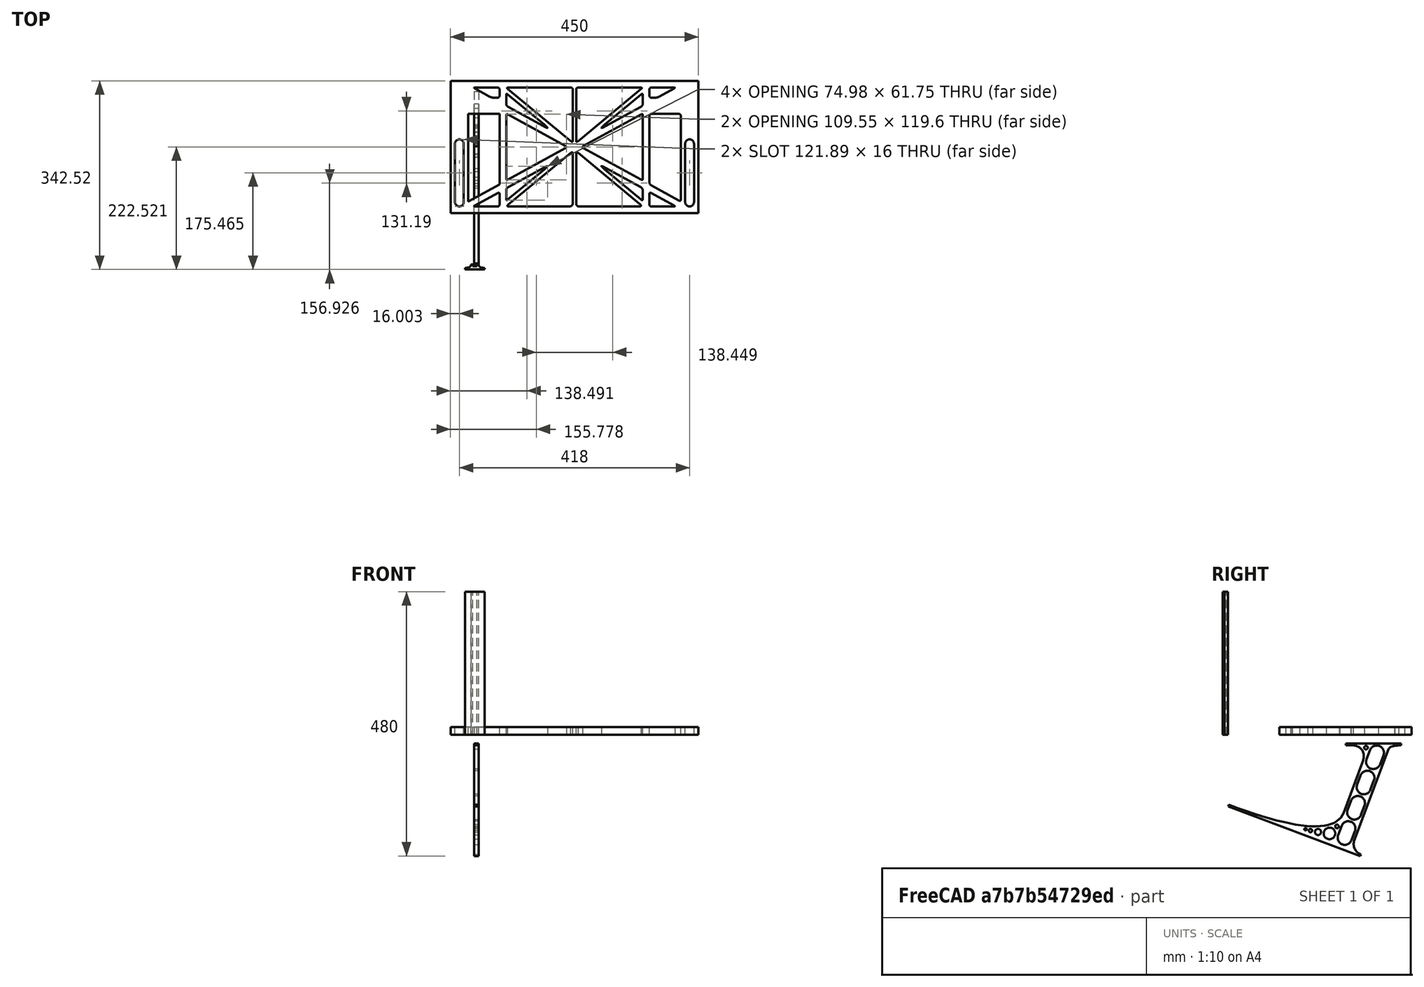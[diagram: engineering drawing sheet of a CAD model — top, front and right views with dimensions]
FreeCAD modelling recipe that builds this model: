
FCSTD DOCUMENT  (FreeCAD 0.19R0.19.2)
Label: laptopStand137FCStd
License: All rights reserved
LicenseURL: http://en.wikipedia.org/wiki/All_rights_reserved
objects: Sketcher::SketchObject×3, Part::Extrusion×3
note: 6 computed .brp shape members not serialized (recipe doc carries the construction recipe); baked Part::Feature solids carry a one-line shape summary decoded from their .brp

FEATURE [Sketcher::SketchObject] Sketch
  FullyConstrained = false
  sketch-geometry (349):
    g0: LineSegment StartX=-10.9272 StartY=-82.7794 StartZ=0 EndX=46.0728 EndY=-51.4823 EndZ=0
    g1: LineSegment StartX=-10.9272 StartY=76.4095 StartZ=0 EndX=-10.9272 EndY=-82.7794 EndZ=0
    g2: LineSegment StartX=46.0728 StartY=76.4095 StartZ=0 EndX=46.0728 EndY=-51.4823 EndZ=0
    g3: LineSegment StartX=-42.9272 StartY=136.221 StartZ=0 EndX=-42.9272 EndY=-103.779 EndZ=0
    g4: LineSegment StartX=407.073 StartY=136.221 StartZ=0 EndX=407.073 EndY=-103.779 EndZ=0
    g5: ArcOfCircle CenterX=-26.9272 CenterY=-83.7794 CenterZ=0 NormalX=0 NormalY=0 NormalZ=1 AngleXU=0 Radius=8 StartAngle=3.14159 EndAngle=6.28319
    g6: ArcOfCircle CenterX=391.073 CenterY=22.1087 CenterZ=0 NormalX=0 NormalY=0 NormalZ=1 AngleXU=0 Radius=8 StartAngle=-4.4e-15 EndAngle=3.14159
    g7: LineSegment StartX=399.073 StartY=22.1087 StartZ=0 EndX=399.073 EndY=-83.7794 EndZ=0
    g8: LineSegment StartX=383.073 StartY=22.1087 StartZ=0 EndX=383.073 EndY=-83.7794 EndZ=0
    g9: ArcOfCircle CenterX=391.073 CenterY=-83.7794 CenterZ=0 NormalX=0 NormalY=0 NormalZ=1 AngleXU=0 Radius=8 StartAngle=3.14159 EndAngle=6.28319
    g10: Circle CenterX=175.022 CenterY=27.0628 CenterZ=0 NormalX=0 NormalY=0 NormalZ=1 AngleXU=0 Radius=1
    g11: Circle CenterX=179.022 CenterY=24.8665 CenterZ=0 NormalX=0 NormalY=0 NormalZ=1 AngleXU=0 Radius=1
    g12: Circle CenterX=179.022 CenterY=27.0628 CenterZ=0 NormalX=0 NormalY=0 NormalZ=1 AngleXU=0 Radius=1
    g13: BSplineCurve PolesCount=3 KnotsCount=2 Degree=2 IsPeriodic=0
    g14: GeomPoint X=175.022 Y=27.0628 Z=0
    g15: GeomPoint X=179.022 Y=27.0628 Z=0
    g16: Circle CenterX=189.124 CenterY=27.0628 CenterZ=0 NormalX=0 NormalY=0 NormalZ=1 AngleXU=0 Radius=1
    g17: Circle CenterX=185.124 CenterY=24.8665 CenterZ=0 NormalX=0 NormalY=0 NormalZ=1 AngleXU=0 Radius=1
    g18: Circle CenterX=185.124 CenterY=27.0628 CenterZ=0 NormalX=0 NormalY=0 NormalZ=1 AngleXU=0 Radius=1
    g19: BSplineCurve PolesCount=3 KnotsCount=2 Degree=2 IsPeriodic=0
    g20: GeomPoint X=189.124 Y=27.0628 Z=0
    g21: GeomPoint X=185.124 Y=27.0628 Z=0
    g22: Circle CenterX=175.022 CenterY=5.37834 CenterZ=0 NormalX=0 NormalY=0 NormalZ=1 AngleXU=0 Radius=1
    g23: Circle CenterX=179.022 CenterY=7.57463 CenterZ=0 NormalX=0 NormalY=0 NormalZ=1 AngleXU=0 Radius=1
    g24: Circle CenterX=179.022 CenterY=5.34704 CenterZ=0 NormalX=0 NormalY=0 NormalZ=1 AngleXU=0 Radius=1
    g25: BSplineCurve PolesCount=3 KnotsCount=2 Degree=2 IsPeriodic=0
    g26: GeomPoint X=175.022 Y=5.37834 Z=0
    g27: GeomPoint X=179.022 Y=5.34704 Z=0
    g28: Circle CenterX=189.124 CenterY=5.37834 CenterZ=0 NormalX=0 NormalY=0 NormalZ=1 AngleXU=0 Radius=1
    g29: Circle CenterX=185.124 CenterY=7.57463 CenterZ=0 NormalX=0 NormalY=0 NormalZ=1 AngleXU=0 Radius=1
    g30: Circle CenterX=185.124 CenterY=5.34704 CenterZ=0 NormalX=0 NormalY=0 NormalZ=1 AngleXU=0 Radius=1
    g31: BSplineCurve PolesCount=3 KnotsCount=2 Degree=2 IsPeriodic=0
    g32: GeomPoint X=189.124 Y=5.37834 Z=0
    g33: GeomPoint X=185.124 Y=5.34704 Z=0
    g34: Circle CenterX=165.871 CenterY=18.1458 CenterZ=0 NormalX=0 NormalY=0 NormalZ=1 AngleXU=0 Radius=1
    g35: Circle CenterX=169.377 CenterY=16.2206 CenterZ=0 NormalX=0 NormalY=0 NormalZ=1 AngleXU=0 Radius=1
    g36: Circle CenterX=165.871 CenterY=14.2954 CenterZ=0 NormalX=0 NormalY=0 NormalZ=1 AngleXU=0 Radius=1
    g37: BSplineCurve PolesCount=3 KnotsCount=2 Degree=2 IsPeriodic=0
    g38: GeomPoint X=165.871 Y=18.1458 Z=0
    g39: GeomPoint X=165.871 Y=14.2954 Z=0
    g40: Circle CenterX=198.275 CenterY=18.1458 CenterZ=0 NormalX=0 NormalY=0 NormalZ=1 AngleXU=0 Radius=1
    g41: Circle CenterX=194.768 CenterY=16.2206 CenterZ=0 NormalX=0 NormalY=0 NormalZ=1 AngleXU=0 Radius=1
    g42: Circle CenterX=198.275 CenterY=14.2954 CenterZ=0 NormalX=0 NormalY=0 NormalZ=1 AngleXU=0 Radius=1
    g43: BSplineCurve PolesCount=3 KnotsCount=2 Degree=2 IsPeriodic=0
    g44: GeomPoint X=198.275 Y=18.1458 Z=0
    g45: GeomPoint X=198.275 Y=14.2954 Z=0
    g46: LineSegment StartX=407.073 StartY=-103.779 StartZ=0 EndX=-42.9272 EndY=-103.779 EndZ=0
    g47: LineSegment StartX=407.073 StartY=136.221 StartZ=0 EndX=-42.9272 EndY=136.221 EndZ=0
    g48: LineSegment StartX=46.0728 StartY=76.4095 StartZ=0 EndX=-10.9272 EndY=76.4095 EndZ=0
    g49: Circle CenterX=125.607 CenterY=54.1951 CenterZ=0 NormalX=0 NormalY=0 NormalZ=1 AngleXU=0 Radius=1
    g50: Circle CenterX=139.632 CenterY=46.4944 CenterZ=0 NormalX=0 NormalY=0 NormalZ=1 AngleXU=0 Radius=1
    g51: Circle CenterX=127.326 CenterY=56.7187 CenterZ=0 NormalX=0 NormalY=0 NormalZ=1 AngleXU=0 Radius=1
    g52: BSplineCurve PolesCount=3 KnotsCount=2 Degree=2 IsPeriodic=0
    g53: GeomPoint X=125.607 Y=54.1951 Z=0
    g54: GeomPoint X=127.326 Y=56.7187 Z=0
    g55: Circle CenterX=236.821 CenterY=56.7187 CenterZ=0 NormalX=0 NormalY=0 NormalZ=1 AngleXU=0 Radius=1
    g56: Circle CenterX=224.513 CenterY=46.4944 CenterZ=0 NormalX=0 NormalY=0 NormalZ=1 AngleXU=0 Radius=1
    g57: Circle CenterX=238.538 CenterY=54.1951 CenterZ=0 NormalX=0 NormalY=0 NormalZ=1 AngleXU=0 Radius=1
    g58: BSplineCurve PolesCount=3 KnotsCount=2 Degree=2 IsPeriodic=0
    g59: GeomPoint X=236.821 Y=56.7187 Z=0
    g60: GeomPoint X=238.538 Y=54.1951 Z=0
    g61: Circle CenterX=238.538 CenterY=-21.7539 CenterZ=0 NormalX=0 NormalY=0 NormalZ=1 AngleXU=0 Radius=1
    g62: Circle CenterX=224.513 CenterY=-14.0532 CenterZ=0 NormalX=0 NormalY=0 NormalZ=1 AngleXU=0 Radius=1
    g63: Circle CenterX=236.821 CenterY=-24.2775 CenterZ=0 NormalX=0 NormalY=0 NormalZ=1 AngleXU=0 Radius=1
    g64: BSplineCurve PolesCount=3 KnotsCount=2 Degree=2 IsPeriodic=0
    g65: GeomPoint X=238.538 Y=-21.7539 Z=0
    g66: GeomPoint X=236.821 Y=-24.2775 Z=0
    g67: Circle CenterX=125.607 CenterY=-21.7539 CenterZ=0 NormalX=0 NormalY=0 NormalZ=1 AngleXU=0 Radius=1
    g68: Circle CenterX=139.632 CenterY=-14.0532 CenterZ=0 NormalX=0 NormalY=0 NormalZ=1 AngleXU=0 Radius=1
    g69: Circle CenterX=127.325 CenterY=-24.2775 CenterZ=0 NormalX=0 NormalY=0 NormalZ=1 AngleXU=0 Radius=1
    g70: BSplineCurve PolesCount=3 KnotsCount=2 Degree=2 IsPeriodic=0
    g71: GeomPoint X=125.607 Y=-21.7539 Z=0
    g72: GeomPoint X=127.325 Y=-24.2775 Z=0
    g73: Circle CenterX=302.996 CenterY=111.695 CenterZ=0 NormalX=0 NormalY=0 NormalZ=1 AngleXU=0 Radius=1
    g74: Circle CenterX=306.073 CenterY=114.251 CenterZ=0 NormalX=0 NormalY=0 NormalZ=1 AngleXU=0 Radius=1
    g75: Circle CenterX=306.073 CenterY=110.251 CenterZ=0 NormalX=0 NormalY=0 NormalZ=1 AngleXU=0 Radius=1
    g76: BSplineCurve PolesCount=3 KnotsCount=2 Degree=2 IsPeriodic=0
    g77: GeomPoint X=302.996 Y=111.695 Z=0
    g78: GeomPoint X=306.073 Y=110.251 Z=0
    g79: Circle CenterX=306.073 CenterY=95.2763 CenterZ=0 NormalX=0 NormalY=0 NormalZ=1 AngleXU=0 Radius=1
    g80: Circle CenterX=306.073 CenterY=91.2763 CenterZ=0 NormalX=0 NormalY=0 NormalZ=1 AngleXU=0 Radius=1
    g81: Circle CenterX=302.567 CenterY=89.3511 CenterZ=0 NormalX=0 NormalY=0 NormalZ=1 AngleXU=0 Radius=1
    g82: BSplineCurve PolesCount=3 KnotsCount=2 Degree=2 IsPeriodic=0
    g83: GeomPoint X=306.073 Y=95.2763 Z=0
    g84: GeomPoint X=302.567 Y=89.3511 Z=0
    g85: LineSegment StartX=306.073 StartY=110.251 StartZ=0 EndX=306.073 EndY=95.2763 EndZ=0
    g86: LineSegment StartX=302.996 StartY=111.695 StartZ=0 EndX=236.821 EndY=56.7187 EndZ=0
    g87: LineSegment StartX=238.538 StartY=54.1951 StartZ=0 EndX=302.567 EndY=89.3511 EndZ=0
    g88: Circle CenterX=61.1496 CenterY=111.695 CenterZ=0 NormalX=0 NormalY=0 NormalZ=1 AngleXU=0 Radius=1
    g89: Circle CenterX=58.0728 CenterY=114.251 CenterZ=0 NormalX=0 NormalY=0 NormalZ=1 AngleXU=0 Radius=1
    g90: Circle CenterX=58.0728 CenterY=110.251 CenterZ=0 NormalX=0 NormalY=0 NormalZ=1 AngleXU=0 Radius=1
    g91: BSplineCurve PolesCount=3 KnotsCount=2 Degree=2 IsPeriodic=0
    g92: GeomPoint X=61.1496 Y=111.695 Z=0
    g93: GeomPoint X=58.0728 Y=110.251 Z=0
    g94: Circle CenterX=61.5791 CenterY=89.3511 CenterZ=0 NormalX=0 NormalY=0 NormalZ=1 AngleXU=0 Radius=1
    g95: Circle CenterX=58.0728 CenterY=91.2763 CenterZ=0 NormalX=0 NormalY=0 NormalZ=1 AngleXU=0 Radius=1
    g96: Circle CenterX=58.0728 CenterY=95.2763 CenterZ=0 NormalX=0 NormalY=0 NormalZ=1 AngleXU=0 Radius=1
    g97: BSplineCurve PolesCount=3 KnotsCount=2 Degree=2 IsPeriodic=0
    g98: GeomPoint X=61.5791 Y=89.3511 Z=0
    g99: GeomPoint X=58.0728 Y=95.2763 Z=0
    g100: LineSegment StartX=58.0728 StartY=110.251 StartZ=0 EndX=58.0728 EndY=95.2763 EndZ=0
    g101: LineSegment StartX=61.1496 StartY=111.695 StartZ=0 EndX=127.326 EndY=56.7187 EndZ=0
    g102: LineSegment StartX=125.607 StartY=54.1951 StartZ=0 EndX=61.5791 EndY=89.3511 EndZ=0
    g103: Circle CenterX=61.5791 CenterY=-56.9099 CenterZ=0 NormalX=0 NormalY=0 NormalZ=1 AngleXU=0 Radius=1
    g104: Circle CenterX=58.0728 CenterY=-58.8351 CenterZ=0 NormalX=0 NormalY=0 NormalZ=1 AngleXU=0 Radius=1
    g105: Circle CenterX=58.0728 CenterY=-62.8351 CenterZ=0 NormalX=0 NormalY=0 NormalZ=1 AngleXU=0 Radius=1
    g106: BSplineCurve PolesCount=3 KnotsCount=2 Degree=2 IsPeriodic=0
    g107: GeomPoint X=61.5791 Y=-56.9099 Z=0
    g108: GeomPoint X=58.0728 Y=-62.8351 Z=0
    g109: Circle CenterX=58.0728 CenterY=-77.8102 CenterZ=0 NormalX=0 NormalY=0 NormalZ=1 AngleXU=0 Radius=1
    g110: Circle CenterX=58.0728 CenterY=-81.8102 CenterZ=0 NormalX=0 NormalY=0 NormalZ=1 AngleXU=0 Radius=1
    g111: Circle CenterX=61.1496 CenterY=-79.2541 CenterZ=0 NormalX=0 NormalY=0 NormalZ=1 AngleXU=0 Radius=1
    g112: BSplineCurve PolesCount=3 KnotsCount=2 Degree=2 IsPeriodic=0
    g113: GeomPoint X=58.0728 Y=-77.8102 Z=0
    g114: GeomPoint X=61.1496 Y=-79.2541 Z=0
    g115: LineSegment StartX=58.0728 StartY=-62.8351 StartZ=0 EndX=58.0728 EndY=-77.8102 EndZ=0
    g116: LineSegment StartX=61.1496 StartY=-79.2541 StartZ=0 EndX=127.325 EndY=-24.2775 EndZ=0
    g117: LineSegment StartX=125.607 StartY=-21.7539 StartZ=0 EndX=61.5791 EndY=-56.9099 EndZ=0
    g118: Circle CenterX=302.567 CenterY=-56.9099 CenterZ=0 NormalX=0 NormalY=0 NormalZ=1 AngleXU=0 Radius=1
    g119: Circle CenterX=306.073 CenterY=-58.8351 CenterZ=0 NormalX=0 NormalY=0 NormalZ=1 AngleXU=0 Radius=1
    g120: Circle CenterX=306.073 CenterY=-62.8351 CenterZ=0 NormalX=0 NormalY=0 NormalZ=1 AngleXU=0 Radius=1
    g121: BSplineCurve PolesCount=3 KnotsCount=2 Degree=2 IsPeriodic=0
    g122: GeomPoint X=302.567 Y=-56.9099 Z=0
    g123: GeomPoint X=306.073 Y=-62.8351 Z=0
    g124: Circle CenterX=302.996 CenterY=-79.2541 CenterZ=0 NormalX=0 NormalY=0 NormalZ=1 AngleXU=0 Radius=1
    g125: Circle CenterX=306.073 CenterY=-81.8102 CenterZ=0 NormalX=0 NormalY=0 NormalZ=1 AngleXU=0 Radius=1
    g126: Circle CenterX=306.073 CenterY=-77.8102 CenterZ=0 NormalX=0 NormalY=0 NormalZ=1 AngleXU=0 Radius=1
    g127: BSplineCurve PolesCount=3 KnotsCount=2 Degree=2 IsPeriodic=0
    g128: GeomPoint X=302.996 Y=-79.2541 Z=0
    g129: GeomPoint X=306.073 Y=-77.8102 Z=0
    g130: LineSegment StartX=306.073 StartY=-62.8351 StartZ=0 EndX=306.073 EndY=-77.8102 EndZ=0
    g131: LineSegment StartX=302.996 StartY=-79.2541 StartZ=0 EndX=236.821 EndY=-24.2775 EndZ=0
    g132: LineSegment StartX=238.538 StartY=-21.7539 StartZ=0 EndX=302.567 EndY=-56.9099 EndZ=0
    g133: Circle CenterX=61.6457 CenterY=-88.8112 CenterZ=0 NormalX=0 NormalY=0 NormalZ=1 AngleXU=0 Radius=1
    g134: Circle CenterX=58.0728 CenterY=-91.7794 CenterZ=0 NormalX=0 NormalY=0 NormalZ=1 AngleXU=0 Radius=1
    g135: Circle CenterX=63.9135 CenterY=-91.7794 CenterZ=0 NormalX=0 NormalY=0 NormalZ=1 AngleXU=0 Radius=1
    g136: BSplineCurve PolesCount=3 KnotsCount=2 Degree=2 IsPeriodic=0
    g137: GeomPoint X=61.6457 Y=-88.8112 Z=0
    g138: GeomPoint X=63.9135 Y=-91.7794 Z=0
    g139: Circle CenterX=179.022 CenterY=-85.8163 CenterZ=0 NormalX=0 NormalY=0 NormalZ=1 AngleXU=0 Radius=1
    g140: Circle CenterX=179.022 CenterY=-91.7794 CenterZ=0 NormalX=0 NormalY=0 NormalZ=1 AngleXU=0 Radius=1
    g141: Circle CenterX=171.895 CenterY=-91.7794 CenterZ=0 NormalX=0 NormalY=0 NormalZ=1 AngleXU=0 Radius=1
    g142: BSplineCurve PolesCount=3 KnotsCount=2 Degree=2 IsPeriodic=0
    g143: GeomPoint X=179.022 Y=-85.8163 Z=0
    g144: GeomPoint X=171.895 Y=-91.7794 Z=0
    g145: Circle CenterX=185.124 CenterY=-86.2028 CenterZ=0 NormalX=0 NormalY=0 NormalZ=1 AngleXU=0 Radius=1
    g146: Circle CenterX=185.124 CenterY=-91.7794 CenterZ=0 NormalX=0 NormalY=0 NormalZ=1 AngleXU=0 Radius=1
    g147: Circle CenterX=191.747 CenterY=-91.7794 CenterZ=0 NormalX=0 NormalY=0 NormalZ=1 AngleXU=0 Radius=1
    g148: BSplineCurve PolesCount=3 KnotsCount=2 Degree=2 IsPeriodic=0
    g149: GeomPoint X=185.124 Y=-86.2028 Z=0
    g150: GeomPoint X=191.747 Y=-91.7794 Z=0
    g151: Circle CenterX=299.888 CenterY=-86.6413 CenterZ=0 NormalX=0 NormalY=0 NormalZ=1 AngleXU=0 Radius=1
    g152: Circle CenterX=306.073 CenterY=-91.7794 CenterZ=0 NormalX=0 NormalY=0 NormalZ=1 AngleXU=0 Radius=1
    g153: Circle CenterX=298.776 CenterY=-91.7794 CenterZ=0 NormalX=0 NormalY=0 NormalZ=1 AngleXU=0 Radius=1
    g154: BSplineCurve PolesCount=3 KnotsCount=2 Degree=2 IsPeriodic=0
    g155: GeomPoint X=299.888 Y=-86.6413 Z=0
    g156: GeomPoint X=298.776 Y=-91.7794 Z=0
    g157: LineSegment StartX=189.124 StartY=5.37834 StartZ=0 EndX=299.888 EndY=-86.6413 EndZ=0
    g158: LineSegment StartX=298.776 StartY=-91.7794 StartZ=0 EndX=191.747 EndY=-91.7794 EndZ=0
    g159: LineSegment StartX=185.124 StartY=-86.2028 StartZ=0 EndX=185.124 EndY=5.34704 EndZ=0
    g160: LineSegment StartX=179.022 StartY=5.34704 StartZ=0 EndX=179.022 EndY=-85.8163 EndZ=0
    g161: LineSegment StartX=171.895 StartY=-91.7794 StartZ=0 EndX=63.9135 EndY=-91.7794 EndZ=0
    g162: LineSegment StartX=61.6457 StartY=-88.8112 StartZ=0 EndX=175.022 EndY=5.37834 EndZ=0
    g163: Circle CenterX=302.073 CenterY=124.221 CenterZ=0 NormalX=0 NormalY=0 NormalZ=1 AngleXU=0 Radius=1
    g164: Circle CenterX=306.073 CenterY=124.221 CenterZ=0 NormalX=0 NormalY=0 NormalZ=1 AngleXU=0 Radius=1
    g165: Circle CenterX=302.996 CenterY=121.665 CenterZ=0 NormalX=0 NormalY=0 NormalZ=1 AngleXU=0 Radius=1
    g166: BSplineCurve PolesCount=3 KnotsCount=2 Degree=2 IsPeriodic=0
    g167: GeomPoint X=302.073 Y=124.221 Z=0
    g168: GeomPoint X=302.996 Y=121.665 Z=0
    g169: Circle CenterX=189.124 CenterY=124.221 CenterZ=0 NormalX=0 NormalY=0 NormalZ=1 AngleXU=0 Radius=1
    g170: Circle CenterX=185.124 CenterY=124.221 CenterZ=0 NormalX=0 NormalY=0 NormalZ=1 AngleXU=0 Radius=1
    g171: Circle CenterX=185.124 CenterY=120.221 CenterZ=0 NormalX=0 NormalY=0 NormalZ=1 AngleXU=0 Radius=1
    g172: BSplineCurve PolesCount=3 KnotsCount=2 Degree=2 IsPeriodic=0
    g173: GeomPoint X=189.124 Y=124.221 Z=0
    g174: GeomPoint X=185.124 Y=120.221 Z=0
    g175: Circle CenterX=175.022 CenterY=124.221 CenterZ=0 NormalX=0 NormalY=0 NormalZ=1 AngleXU=0 Radius=1
    g176: Circle CenterX=179.022 CenterY=124.221 CenterZ=0 NormalX=0 NormalY=0 NormalZ=1 AngleXU=0 Radius=1
    g177: Circle CenterX=179.022 CenterY=120.221 CenterZ=0 NormalX=0 NormalY=0 NormalZ=1 AngleXU=0 Radius=1
    g178: BSplineCurve PolesCount=3 KnotsCount=2 Degree=2 IsPeriodic=0
    g179: GeomPoint X=175.022 Y=124.221 Z=0
    g180: GeomPoint X=179.022 Y=120.221 Z=0
    g181: Circle CenterX=62.0728 CenterY=124.221 CenterZ=0 NormalX=0 NormalY=0 NormalZ=1 AngleXU=0 Radius=1
    g182: Circle CenterX=58.0728 CenterY=124.221 CenterZ=0 NormalX=0 NormalY=0 NormalZ=1 AngleXU=0 Radius=1
    g183: Circle CenterX=61.1496 CenterY=121.665 CenterZ=0 NormalX=0 NormalY=0 NormalZ=1 AngleXU=0 Radius=1
    g184: BSplineCurve PolesCount=3 KnotsCount=2 Degree=2 IsPeriodic=0
    g185: GeomPoint X=62.0728 Y=124.221 Z=0
    g186: GeomPoint X=61.1496 Y=121.665 Z=0
    g187: LineSegment StartX=62.0728 StartY=124.221 StartZ=0 EndX=175.022 EndY=124.221 EndZ=0
    g188: LineSegment StartX=179.022 StartY=120.221 StartZ=0 EndX=179.022 EndY=27.0628 EndZ=0
    g189: LineSegment StartX=185.124 StartY=27.0628 StartZ=0 EndX=185.124 EndY=120.221 EndZ=0
    g190: LineSegment StartX=189.124 StartY=124.221 StartZ=0 EndX=302.073 EndY=124.221 EndZ=0
    g191: LineSegment StartX=302.996 StartY=121.665 StartZ=0 EndX=189.124 EndY=27.0628 EndZ=0
    g192: LineSegment StartX=175.022 StartY=27.0628 StartZ=0 EndX=61.1496 EndY=121.665 EndZ=0
    g193: Circle CenterX=61.5791 CenterY=75.4095 CenterZ=0 NormalX=0 NormalY=0 NormalZ=1 AngleXU=0 Radius=1
    g194: Circle CenterX=58.0728 CenterY=77.3346 CenterZ=0 NormalX=0 NormalY=0 NormalZ=1 AngleXU=0 Radius=1
    g195: Circle CenterX=58.0728 CenterY=73.3346 CenterZ=0 NormalX=0 NormalY=0 NormalZ=1 AngleXU=0 Radius=1
    g196: BSplineCurve PolesCount=3 KnotsCount=2 Degree=2 IsPeriodic=0
    g197: GeomPoint X=61.5791 Y=75.4095 Z=0
    g198: GeomPoint X=58.0728 Y=73.3346 Z=0
    g199: Circle CenterX=58.0728 CenterY=-40.8935 CenterZ=0 NormalX=0 NormalY=0 NormalZ=1 AngleXU=0 Radius=1
    g200: Circle CenterX=58.0728 CenterY=-44.8935 CenterZ=0 NormalX=0 NormalY=0 NormalZ=1 AngleXU=0 Radius=1
    g201: Circle CenterX=61.5791 CenterY=-42.9683 CenterZ=0 NormalX=0 NormalY=0 NormalZ=1 AngleXU=0 Radius=1
    g202: BSplineCurve PolesCount=3 KnotsCount=2 Degree=2 IsPeriodic=0
    g203: GeomPoint X=58.0728 Y=-40.8935 Z=0
    g204: GeomPoint X=61.5791 Y=-42.9683 Z=0
    g205: LineSegment StartX=61.5791 StartY=-42.9683 StartZ=0 EndX=165.871 EndY=14.2954 EndZ=0
    g206: LineSegment StartX=165.871 StartY=18.1458 StartZ=0 EndX=61.5791 EndY=75.4095 EndZ=0
    g207: LineSegment StartX=58.0728 StartY=73.3346 StartZ=0 EndX=58.0728 EndY=-40.8935 EndZ=0
    g208: Circle CenterX=302.567 CenterY=-42.9683 CenterZ=0 NormalX=0 NormalY=0 NormalZ=1 AngleXU=0 Radius=1
    g209: Circle CenterX=306.073 CenterY=-44.8935 CenterZ=0 NormalX=0 NormalY=0 NormalZ=1 AngleXU=0 Radius=1
    g210: Circle CenterX=306.073 CenterY=-40.8935 CenterZ=0 NormalX=0 NormalY=0 NormalZ=1 AngleXU=0 Radius=1
    g211: BSplineCurve PolesCount=3 KnotsCount=2 Degree=2 IsPeriodic=0
    g212: GeomPoint X=302.567 Y=-42.9683 Z=0
    g213: GeomPoint X=306.073 Y=-40.8935 Z=0
    g214: Circle CenterX=306.073 CenterY=73.3346 CenterZ=0 NormalX=0 NormalY=0 NormalZ=1 AngleXU=0 Radius=1
    g215: Circle CenterX=306.073 CenterY=77.3346 CenterZ=0 NormalX=0 NormalY=0 NormalZ=1 AngleXU=0 Radius=1
    g216: Circle CenterX=302.567 CenterY=75.4095 CenterZ=0 NormalX=0 NormalY=0 NormalZ=1 AngleXU=0 Radius=1
    g217: BSplineCurve PolesCount=3 KnotsCount=2 Degree=2 IsPeriodic=0
    g218: GeomPoint X=306.073 Y=73.3346 Z=0
    g219: GeomPoint X=302.567 Y=75.4095 Z=0
    g220: LineSegment StartX=302.567 StartY=-42.9683 StartZ=0 EndX=198.275 EndY=14.2954 EndZ=0
    g221: LineSegment StartX=198.275 StartY=18.1458 StartZ=0 EndX=302.567 EndY=75.4095 EndZ=0
    g222: LineSegment StartX=306.073 StartY=73.3346 StartZ=0 EndX=306.073 EndY=-40.8935 EndZ=0
    g223: LineSegment StartX=322.073 StartY=105.865 StartZ=0 EndX=328.643 EndY=105.865 EndZ=0
    g224: LineSegment StartX=318.073 StartY=120.221 StartZ=0 EndX=318.073 EndY=109.865 EndZ=0
    g225: LineSegment StartX=336.157 StartY=107.779 StartZ=0 EndX=362.567 EndY=122.294 EndZ=0
    g226: Circle CenterX=362.073 CenterY=124.221 CenterZ=0 NormalX=0 NormalY=0 NormalZ=1 AngleXU=0 Radius=1
    g227: Circle CenterX=366.073 CenterY=124.221 CenterZ=0 NormalX=0 NormalY=0 NormalZ=1 AngleXU=0 Radius=1
    g228: Circle CenterX=362.567 CenterY=122.294 CenterZ=0 NormalX=0 NormalY=0 NormalZ=1 AngleXU=0 Radius=1
    g229: BSplineCurve PolesCount=3 KnotsCount=2 Degree=2 IsPeriodic=0
    g230: GeomPoint X=362.073 Y=124.221 Z=0
    g231: GeomPoint X=362.567 Y=122.294 Z=0
    g232: Circle CenterX=322.073 CenterY=124.221 CenterZ=0 NormalX=0 NormalY=0 NormalZ=1 AngleXU=0 Radius=1
    g233: Circle CenterX=318.073 CenterY=124.221 CenterZ=0 NormalX=0 NormalY=0 NormalZ=1 AngleXU=0 Radius=1
    g234: Circle CenterX=318.073 CenterY=120.221 CenterZ=0 NormalX=0 NormalY=0 NormalZ=1 AngleXU=0 Radius=1
    g235: BSplineCurve PolesCount=3 KnotsCount=2 Degree=2 IsPeriodic=0
    g236: GeomPoint X=322.073 Y=124.221 Z=0
    g237: GeomPoint X=318.073 Y=120.221 Z=0
    g238: Circle CenterX=322.073 CenterY=105.865 CenterZ=0 NormalX=0 NormalY=0 NormalZ=1 AngleXU=0 Radius=1
    g239: Circle CenterX=318.073 CenterY=105.865 CenterZ=0 NormalX=0 NormalY=0 NormalZ=1 AngleXU=0 Radius=1
    g240: Circle CenterX=318.073 CenterY=109.865 CenterZ=0 NormalX=0 NormalY=0 NormalZ=1 AngleXU=0 Radius=1
    g241: BSplineCurve PolesCount=3 KnotsCount=2 Degree=2 IsPeriodic=0
    g242: GeomPoint X=322.073 Y=105.865 Z=0
    g243: GeomPoint X=318.073 Y=109.865 Z=0
    g244: Circle CenterX=336.157 CenterY=107.779 CenterZ=0 NormalX=0 NormalY=0 NormalZ=1 AngleXU=0 Radius=1
    g245: Circle CenterX=332.651 CenterY=105.853 CenterZ=0 NormalX=0 NormalY=0 NormalZ=1 AngleXU=0 Radius=1
    g246: Circle CenterX=328.643 CenterY=105.865 CenterZ=0 NormalX=0 NormalY=0 NormalZ=1 AngleXU=0 Radius=1
    g247: BSplineCurve PolesCount=3 KnotsCount=2 Degree=2 IsPeriodic=0
    g248: GeomPoint X=336.157 Y=107.779 Z=0
    g249: GeomPoint X=328.643 Y=105.865 Z=0
    g250: LineSegment StartX=322.073 StartY=124.221 StartZ=0 EndX=362.073 EndY=124.221 EndZ=0
    g251: Circle CenterX=371.567 CenterY=-80.8644 CenterZ=0 NormalX=0 NormalY=0 NormalZ=1 AngleXU=0 Radius=1
    g252: Circle CenterX=375.073 CenterY=-82.7896 CenterZ=0 NormalX=0 NormalY=0 NormalZ=1 AngleXU=0 Radius=1
    g253: Circle CenterX=375.073 CenterY=-78.7896 CenterZ=0 NormalX=0 NormalY=0 NormalZ=1 AngleXU=0 Radius=1
    g254: BSplineCurve PolesCount=3 KnotsCount=2 Degree=2 IsPeriodic=0
    g255: GeomPoint X=371.567 Y=-80.8644 Z=0
    g256: GeomPoint X=375.073 Y=-78.7896 Z=0
    g257: Circle CenterX=321.579 CenterY=-53.4075 CenterZ=0 NormalX=0 NormalY=0 NormalZ=1 AngleXU=0 Radius=1
    g258: Circle CenterX=318.073 CenterY=-51.4823 CenterZ=0 NormalX=0 NormalY=0 NormalZ=1 AngleXU=0 Radius=1
    g259: Circle CenterX=318.073 CenterY=-47.4823 CenterZ=0 NormalX=0 NormalY=0 NormalZ=1 AngleXU=0 Radius=1
    g260: BSplineCurve PolesCount=3 KnotsCount=2 Degree=2 IsPeriodic=0
    g261: GeomPoint X=321.579 Y=-53.4075 Z=0
    g262: GeomPoint X=318.073 Y=-47.4823 Z=0
    g263: LineSegment StartX=371.567 StartY=-80.8644 StartZ=0 EndX=321.579 EndY=-53.4075 EndZ=0
    g264: Circle CenterX=321.579 CenterY=-67.3492 CenterZ=0 NormalX=0 NormalY=0 NormalZ=1 AngleXU=0 Radius=1
    g265: Circle CenterX=318.073 CenterY=-65.424 CenterZ=0 NormalX=0 NormalY=0 NormalZ=1 AngleXU=0 Radius=1
    g266: Circle CenterX=318.073 CenterY=-69.424 CenterZ=0 NormalX=0 NormalY=0 NormalZ=1 AngleXU=0 Radius=1
    g267: BSplineCurve PolesCount=3 KnotsCount=2 Degree=2 IsPeriodic=0
    g268: GeomPoint X=321.579 Y=-67.3492 Z=0
    g269: GeomPoint X=318.073 Y=-69.424 Z=0
    g270: Circle CenterX=362.567 CenterY=-89.8542 CenterZ=0 NormalX=0 NormalY=0 NormalZ=1 AngleXU=0 Radius=1
    g271: Circle CenterX=366.073 CenterY=-91.7794 CenterZ=0 NormalX=0 NormalY=0 NormalZ=1 AngleXU=0 Radius=1
    g272: Circle CenterX=362.073 CenterY=-91.7794 CenterZ=0 NormalX=0 NormalY=0 NormalZ=1 AngleXU=0 Radius=1
    g273: BSplineCurve PolesCount=3 KnotsCount=2 Degree=2 IsPeriodic=0
    g274: GeomPoint X=362.567 Y=-89.8542 Z=0
    g275: GeomPoint X=362.073 Y=-91.7794 Z=0
    g276: Circle CenterX=322.073 CenterY=-91.7794 CenterZ=0 NormalX=0 NormalY=0 NormalZ=1 AngleXU=0 Radius=1
    g277: Circle CenterX=318.073 CenterY=-91.7794 CenterZ=0 NormalX=0 NormalY=0 NormalZ=1 AngleXU=0 Radius=1
    g278: Circle CenterX=318.073 CenterY=-87.7794 CenterZ=0 NormalX=0 NormalY=0 NormalZ=1 AngleXU=0 Radius=1
    g279: BSplineCurve PolesCount=3 KnotsCount=2 Degree=2 IsPeriodic=0
    g280: GeomPoint X=322.073 Y=-91.7794 Z=0
    g281: GeomPoint X=318.073 Y=-87.7794 Z=0
    g282: LineSegment StartX=362.567 StartY=-89.8542 StartZ=0 EndX=321.579 EndY=-67.3492 EndZ=0
    g283: LineSegment StartX=318.073 StartY=-69.424 StartZ=0 EndX=318.073 EndY=-87.7794 EndZ=0
    g284: LineSegment StartX=322.073 StartY=-91.7794 StartZ=0 EndX=362.073 EndY=-91.7794 EndZ=0
    g285: Circle CenterX=2.07281 CenterY=124.221 CenterZ=0 NormalX=0 NormalY=0 NormalZ=1 AngleXU=0 Radius=1
    g286: Circle CenterX=1.57905 CenterY=122.295 CenterZ=0 NormalX=0 NormalY=0 NormalZ=1 AngleXU=0 Radius=1
    g287: BSplineCurve PolesCount=3 KnotsCount=2 Degree=2 IsPeriodic=0
    g288: GeomPoint X=2.07281 Y=124.221 Z=0
    g289: GeomPoint X=1.57905 Y=122.295 Z=0
    g290: Circle CenterX=42.0728 CenterY=124.221 CenterZ=0 NormalX=0 NormalY=0 NormalZ=1 AngleXU=0 Radius=1
    g291: Circle CenterX=46.0728 CenterY=124.221 CenterZ=0 NormalX=0 NormalY=0 NormalZ=1 AngleXU=0 Radius=1
    g292: Circle CenterX=46.0728 CenterY=120.221 CenterZ=0 NormalX=0 NormalY=0 NormalZ=1 AngleXU=0 Radius=1
    g293: BSplineCurve PolesCount=3 KnotsCount=2 Degree=2 IsPeriodic=0
    g294: GeomPoint X=42.0728 Y=124.221 Z=0
    g295: GeomPoint X=46.0728 Y=120.221 Z=0
    g296: Circle CenterX=46.0728 CenterY=109.865 CenterZ=0 NormalX=0 NormalY=0 NormalZ=1 AngleXU=0 Radius=1
    g297: Circle CenterX=46.0728 CenterY=105.865 CenterZ=0 NormalX=0 NormalY=0 NormalZ=1 AngleXU=0 Radius=1
    g298: Circle CenterX=42.0728 CenterY=105.865 CenterZ=0 NormalX=0 NormalY=0 NormalZ=1 AngleXU=0 Radius=1
    g299: BSplineCurve PolesCount=3 KnotsCount=2 Degree=2 IsPeriodic=0
    g300: GeomPoint X=46.0728 Y=109.865 Z=0
    g301: GeomPoint X=42.0728 Y=105.865 Z=0
    g302: Circle CenterX=35.5028 CenterY=105.865 CenterZ=0 NormalX=0 NormalY=0 NormalZ=1 AngleXU=0 Radius=1
    g303: Circle CenterX=31.5028 CenterY=105.865 CenterZ=0 NormalX=0 NormalY=0 NormalZ=1 AngleXU=0 Radius=1
    g304: Circle CenterX=27.9965 CenterY=107.79 CenterZ=0 NormalX=0 NormalY=0 NormalZ=1 AngleXU=0 Radius=1
    g305: BSplineCurve PolesCount=3 KnotsCount=2 Degree=2 IsPeriodic=0
    g306: GeomPoint X=35.5028 Y=105.865 Z=0
    g307: GeomPoint X=27.9965 Y=107.79 Z=0
    g308: LineSegment StartX=2.07281 StartY=124.221 StartZ=0 EndX=42.0728 EndY=124.221 EndZ=0
    g309: LineSegment StartX=46.0728 StartY=120.221 StartZ=0 EndX=46.0728 EndY=109.865 EndZ=0
    g310: LineSegment StartX=42.0728 StartY=105.865 StartZ=0 EndX=35.5028 EndY=105.865 EndZ=0
    g311: LineSegment StartX=27.9965 StartY=107.79 StartZ=0 EndX=1.57905 EndY=122.295 EndZ=0
    g312: Circle CenterX=42.5666 CenterY=-67.3492 CenterZ=0 NormalX=0 NormalY=0 NormalZ=1 AngleXU=0 Radius=1
    g313: Circle CenterX=46.0728 CenterY=-65.424 CenterZ=0 NormalX=0 NormalY=0 NormalZ=1 AngleXU=0 Radius=1
    g314: Circle CenterX=46.0728 CenterY=-69.424 CenterZ=0 NormalX=0 NormalY=0 NormalZ=1 AngleXU=0 Radius=1
    g315: BSplineCurve PolesCount=3 KnotsCount=2 Degree=2 IsPeriodic=0
    g316: GeomPoint X=42.5666 Y=-67.3492 Z=0
    g317: GeomPoint X=46.0728 Y=-69.424 Z=0
    g318: Circle CenterX=46.0728 CenterY=-87.7794 CenterZ=0 NormalX=0 NormalY=0 NormalZ=1 AngleXU=0 Radius=1
    g319: Circle CenterX=46.0728 CenterY=-91.7794 CenterZ=0 NormalX=0 NormalY=0 NormalZ=1 AngleXU=0 Radius=1
    g320: Circle CenterX=42.0728 CenterY=-91.7794 CenterZ=0 NormalX=0 NormalY=0 NormalZ=1 AngleXU=0 Radius=1
    g321: BSplineCurve PolesCount=3 KnotsCount=2 Degree=2 IsPeriodic=0
    g322: GeomPoint X=46.0728 Y=-87.7794 Z=0
    g323: GeomPoint X=42.0728 Y=-91.7794 Z=0
    g324: Circle CenterX=2.07281 CenterY=-91.7794 CenterZ=0 NormalX=0 NormalY=0 NormalZ=1 AngleXU=0 Radius=1
    g325: Circle CenterX=-1.92719 CenterY=-91.7794 CenterZ=0 NormalX=0 NormalY=0 NormalZ=1 AngleXU=0 Radius=1
    g326: Circle CenterX=1.57905 CenterY=-89.8542 CenterZ=0 NormalX=0 NormalY=0 NormalZ=1 AngleXU=0 Radius=1
    g327: BSplineCurve PolesCount=3 KnotsCount=2 Degree=2 IsPeriodic=0
    g328: GeomPoint X=2.07281 Y=-91.7794 Z=0
    g329: GeomPoint X=1.57905 Y=-89.8542 Z=0
    g330: LineSegment StartX=2.07281 StartY=-91.7794 StartZ=0 EndX=42.0728 EndY=-91.7794 EndZ=0
    g331: LineSegment StartX=46.0728 StartY=-87.7794 StartZ=0 EndX=46.0728 EndY=-69.424 EndZ=0
    g332: LineSegment StartX=42.5666 StartY=-67.3492 StartZ=0 EndX=1.57905 EndY=-89.8542 EndZ=0
    g333: Circle CenterX=322.073 CenterY=76.4095 CenterZ=0 NormalX=0 NormalY=0 NormalZ=1 AngleXU=0 Radius=4
    g334: BSplineCurve PolesCount=3 KnotsCount=2 Degree=2 IsPeriodic=0
    g335: GeomPoint X=318.073 Y=72.4095 Z=0
    g336: GeomPoint X=322.073 Y=76.4095 Z=0
    g337: Circle CenterX=375.073 CenterY=72.4095 CenterZ=0 NormalX=0 NormalY=0 NormalZ=1 AngleXU=0 Radius=1
    g338: Circle CenterX=375.073 CenterY=76.4095 CenterZ=0 NormalX=0 NormalY=0 NormalZ=1 AngleXU=0 Radius=1
    g339: Circle CenterX=371.073 CenterY=76.4095 CenterZ=0 NormalX=0 NormalY=0 NormalZ=1 AngleXU=0 Radius=1
    g340: BSplineCurve PolesCount=3 KnotsCount=2 Degree=2 IsPeriodic=0
    g341: GeomPoint X=375.073 Y=72.4095 Z=0
    g342: GeomPoint X=371.073 Y=76.4095 Z=0
    g343: LineSegment StartX=322.073 StartY=76.4095 StartZ=0 EndX=371.073 EndY=76.4095 EndZ=0
    g344: LineSegment StartX=318.073 StartY=72.4095 StartZ=0 EndX=318.073 EndY=-47.4823 EndZ=0
    g345: LineSegment StartX=375.073 StartY=72.4095 StartZ=0 EndX=375.073 EndY=-78.7896 EndZ=0
    g346: ArcOfCircle CenterX=-26.9272 CenterY=22.1087 CenterZ=0 NormalX=0 NormalY=0 NormalZ=1 AngleXU=0 Radius=4 StartAngle=5e-16 EndAngle=3.14159
    g347: LineSegment StartX=-30.9272 StartY=22.1087 StartZ=0 EndX=-34.9272 EndY=-83.7794 EndZ=0
    g348: LineSegment StartX=-18.9272 StartY=-83.7794 StartZ=0 EndX=-22.9272 EndY=22.1087 EndZ=0
  constraints (571):
    c: Coincident(g0,g2)
    c: Block(g0)
    c: Block(g1)
    c: Vertical(g3)
    c: Vertical(g4)
    c: Block(g4)
    c: Block(g3)
    c: Tangent(g6,g7) = 1.5708
    c: Tangent(g7,g9) = 1.5708
    c: Equal(g6,g9)
    c: Coincident(g8,g6)
    c: Coincident(g8,g9)
    c: Block(g7)
    c: Block(g8)
    c: Weight(g10) = 1
    c: Equal(g10,g11)
    c: Equal(g10,g12)
    c: InternalAlignment(g10,g13)
    c: InternalAlignment(g11,g13)
    c: InternalAlignment(g12,g13)
    c: InternalAlignment(g14,g13)
    c: InternalAlignment(g15,g13)
    c: Weight(g16) = 1
    c: Equal(g16,g17)
    c: Equal(g16,g18)
    c: InternalAlignment(g16,g19)
    c: InternalAlignment(g17,g19)
    c: InternalAlignment(g18,g19)
    c: InternalAlignment(g20,g19)
    c: InternalAlignment(g21,g19)
    c: Block(g19)
    c: Block(g13)
    c: Weight(g22) = 1
    c: Equal(g22,g23)
    c: Equal(g22,g24)
    c: InternalAlignment(g22,g25)
    c: InternalAlignment(g23,g25)
    c: InternalAlignment(g24,g25)
    c: InternalAlignment(g26,g25)
    c: InternalAlignment(g27,g25)
    c: Weight(g28) = 1
    c: Equal(g28,g29)
    c: Equal(g28,g30)
    c: InternalAlignment(g28,g31)
    c: InternalAlignment(g29,g31)
    c: InternalAlignment(g30,g31)
    c: InternalAlignment(g32,g31)
    c: InternalAlignment(g33,g31)
    c: Block(g31)
    c: Block(g25)
    c: Weight(g34) = 1
    c: Equal(g34,g35)
    c: Equal(g34,g36)
    c: InternalAlignment(g34,g37)
    c: InternalAlignment(g35,g37)
    c: InternalAlignment(g36,g37)
    c: InternalAlignment(g38,g37)
    c: InternalAlignment(g39,g37)
    c: Weight(g40) = 1
    c: Equal(g40,g41)
    c: Equal(g40,g42)
    c: InternalAlignment(g40,g43)
    c: InternalAlignment(g41,g43)
    c: InternalAlignment(g42,g43)
    c: InternalAlignment(g44,g43)
    c: InternalAlignment(g45,g43)
    c: Block(g37)
    c: Block(g43)
    c: Coincident(g46,g4)
    c: Coincident(g46,g3)
    c: Horizontal(g46)
    c: Distance(g46) = 450
    c: Coincident(g47,g4)
    c: Coincident(g47,g3)
    c: Horizontal(g47)
    c: Horizontal(g48)
    c: Coincident(g2,g48)
    c: Block(g48)
    c: Coincident(g1,g48)
    c: Weight(g49) = 1
    c: Equal(g49,g50)
    c: Equal(g49,g51)
    c: InternalAlignment(g49,g52)
    c: InternalAlignment(g50,g52)
    c: InternalAlignment(g51,g52)
    c: InternalAlignment(g53,g52)
    c: InternalAlignment(g54,g52)
    c: Block(g52)
    c: Weight(g55) = 1
    c: Equal(g55,g56)
    c: Equal(g55,g57)
    c: InternalAlignment(g55,g58)
    c: InternalAlignment(g56,g58)
    c: InternalAlignment(g57,g58)
    c: InternalAlignment(g59,g58)
    c: InternalAlignment(g60,g58)
    c: Block(g58)
    c: Weight(g61) = 1
    c: Equal(g61,g62)
    c: Equal(g61,g63)
    c: InternalAlignment(g61,g64)
    c: InternalAlignment(g62,g64)
    c: InternalAlignment(g63,g64)
    c: InternalAlignment(g65,g64)
    c: InternalAlignment(g66,g64)
    c: Block(g64)
    c: Weight(g67) = 1
    c: Equal(g67,g68)
    c: Equal(g67,g69)
    c: InternalAlignment(g67,g70)
    c: InternalAlignment(g68,g70)
    c: InternalAlignment(g69,g70)
    c: InternalAlignment(g71,g70)
    c: InternalAlignment(g72,g70)
    c: Block(g70)
    c: Weight(g73) = 1
    c: Equal(g73,g74)
    c: Equal(g73,g75)
    c: InternalAlignment(g73,g76)
    c: InternalAlignment(g74,g76)
    c: InternalAlignment(g75,g76)
    c: InternalAlignment(g77,g76)
    c: InternalAlignment(g78,g76)
    c: Weight(g79) = 1
    c: Equal(g79,g80)
    c: Equal(g79,g81)
    c: InternalAlignment(g79,g82)
    c: InternalAlignment(g80,g82)
    c: InternalAlignment(g81,g82)
    c: InternalAlignment(g83,g82)
    c: InternalAlignment(g84,g82)
    c: Block(g76)
    c: Block(g82)
    c: Coincident(g85,g76)
    c: Coincident(g85,g82)
    c: Vertical(g85)
    c: Coincident(g86,g76)
    c: Coincident(g86,g58)
    c: Coincident(g87,g58)
    c: Coincident(g87,g82)
    c: Weight(g88) = 1
    c: Equal(g88,g89)
    c: Equal(g88,g90)
    c: InternalAlignment(g88,g91)
    c: InternalAlignment(g89,g91)
    c: InternalAlignment(g90,g91)
    c: InternalAlignment(g92,g91)
    c: InternalAlignment(g93,g91)
    c: Weight(g94) = 1
    c: Equal(g94,g95)
    c: Equal(g94,g96)
    c: InternalAlignment(g94,g97)
    c: InternalAlignment(g95,g97)
    c: InternalAlignment(g96,g97)
    c: InternalAlignment(g98,g97)
    c: InternalAlignment(g99,g97)
    c: Block(g91)
    c: Block(g97)
    c: Coincident(g100,g91)
    c: Coincident(g100,g97)
    c: Vertical(g100)
    c: Coincident(g101,g91)
    c: Coincident(g101,g52)
    c: Coincident(g102,g52)
    c: Coincident(g102,g97)
    c: Weight(g103) = 1
    c: Equal(g103,g104)
    c: Equal(g103,g105)
    c: InternalAlignment(g103,g106)
    c: InternalAlignment(g104,g106)
    c: InternalAlignment(g105,g106)
    c: InternalAlignment(g107,g106)
    c: InternalAlignment(g108,g106)
    c: Weight(g109) = 1
    c: Equal(g109,g110)
    c: Equal(g109,g111)
    c: InternalAlignment(g109,g112)
    c: InternalAlignment(g110,g112)
    c: InternalAlignment(g111,g112)
    c: InternalAlignment(g113,g112)
    c: InternalAlignment(g114,g112)
    c: Block(g106)
    c: Block(g112)
    c: Coincident(g115,g106)
    c: Coincident(g115,g112)
    c: Vertical(g115)
    c: Coincident(g116,g112)
    c: Coincident(g116,g70)
    c: Coincident(g117,g70)
    c: Coincident(g117,g106)
    c: Weight(g118) = 1
    c: Equal(g118,g119)
    c: Equal(g118,g120)
    c: InternalAlignment(g118,g121)
    c: InternalAlignment(g119,g121)
    c: InternalAlignment(g120,g121)
    c: InternalAlignment(g122,g121)
    c: InternalAlignment(g123,g121)
    c: Weight(g124) = 1
    c: Equal(g124,g125)
    c: Equal(g124,g126)
    c: InternalAlignment(g124,g127)
    c: InternalAlignment(g125,g127)
    c: InternalAlignment(g126,g127)
    c: InternalAlignment(g128,g127)
    c: InternalAlignment(g129,g127)
    c: Block(g121)
    c: Block(g127)
    c: Coincident(g130,g121)
    c: Coincident(g130,g127)
    c: Vertical(g130)
    c: Coincident(g131,g127)
    c: Coincident(g131,g64)
    c: Coincident(g132,g64)
    c: Coincident(g132,g121)
    c: Weight(g133) = 1
    c: Equal(g133,g134)
    c: Equal(g133,g135)
    c: InternalAlignment(g133,g136)
    c: InternalAlignment(g134,g136)
    c: InternalAlignment(g135,g136)
    c: InternalAlignment(g137,g136)
    c: InternalAlignment(g138,g136)
    c: Weight(g139) = 1
    c: Equal(g139,g140)
    c: Equal(g139,g141)
    c: InternalAlignment(g139,g142)
    c: InternalAlignment(g140,g142)
    c: InternalAlignment(g141,g142)
    c: InternalAlignment(g143,g142)
    c: InternalAlignment(g144,g142)
    c: Weight(g145) = 1
    c: Equal(g145,g146)
    c: Equal(g145,g147)
    c: InternalAlignment(g145,g148)
    c: InternalAlignment(g146,g148)
    c: InternalAlignment(g147,g148)
    c: InternalAlignment(g149,g148)
    c: InternalAlignment(g150,g148)
    c: Weight(g151) = 1
    c: Equal(g151,g152)
    c: Equal(g151,g153)
    c: InternalAlignment(g151,g154)
    c: InternalAlignment(g152,g154)
    c: InternalAlignment(g153,g154)
    c: InternalAlignment(g155,g154)
    c: InternalAlignment(g156,g154)
    c: Block(g154)
    c: Block(g148)
    c: Block(g142)
    c: Block(g136)
    c: Coincident(g157,g31)
    c: Coincident(g157,g154)
    c: Coincident(g158,g154)
    c: Coincident(g158,g148)
    c: Horizontal(g158)
    c: Coincident(g159,g148)
    c: Coincident(g159,g31)
    c: Vertical(g159)
    c: Coincident(g160,g25)
    c: Coincident(g160,g142)
    c: Vertical(g160)
    c: Coincident(g161,g142)
    c: Coincident(g161,g136)
    c: Horizontal(g161)
    c: Coincident(g162,g136)
    c: Coincident(g162,g25)
    c: Weight(g163) = 1
    c: Equal(g163,g164)
    c: Equal(g163,g165)
    c: InternalAlignment(g163,g166)
    c: InternalAlignment(g164,g166)
    c: InternalAlignment(g165,g166)
    c: InternalAlignment(g167,g166)
    c: InternalAlignment(g168,g166)
    c: Weight(g169) = 1
    c: Equal(g169,g170)
    c: Equal(g169,g171)
    c: InternalAlignment(g169,g172)
    c: InternalAlignment(g170,g172)
    c: InternalAlignment(g171,g172)
    c: InternalAlignment(g173,g172)
    c: InternalAlignment(g174,g172)
    c: Weight(g175) = 1
    c: Equal(g175,g176)
    c: Equal(g175,g177)
    c: InternalAlignment(g175,g178)
    c: InternalAlignment(g176,g178)
    c: InternalAlignment(g177,g178)
    c: InternalAlignment(g179,g178)
    c: InternalAlignment(g180,g178)
    c: Weight(g181) = 1
    c: Equal(g181,g182)
    c: Equal(g181,g183)
    c: InternalAlignment(g181,g184)
    c: InternalAlignment(g182,g184)
    c: InternalAlignment(g183,g184)
    c: InternalAlignment(g185,g184)
    c: InternalAlignment(g186,g184)
    c: Block(g184)
    c: Block(g178)
    c: Block(g172)
    c: Block(g166)
    c: Coincident(g187,g184)
    c: Coincident(g187,g178)
    c: Horizontal(g187)
    c: Coincident(g188,g178)
    c: Coincident(g188,g13)
    c: Vertical(g188)
    c: Coincident(g189,g19)
    c: Coincident(g189,g172)
    c: Vertical(g189)
    c: Coincident(g190,g172)
    c: Coincident(g190,g166)
    c: Horizontal(g190)
    c: Coincident(g191,g166)
    c: Coincident(g191,g19)
    c: Coincident(g192,g13)
    c: Weight(g193) = 1
    c: Equal(g193,g194)
    c: Equal(g193,g195)
    c: InternalAlignment(g193,g196)
    c: InternalAlignment(g194,g196)
    c: InternalAlignment(g195,g196)
    c: InternalAlignment(g197,g196)
    c: InternalAlignment(g198,g196)
    c: Weight(g199) = 1
    c: Equal(g199,g200)
    c: Equal(g199,g201)
    c: InternalAlignment(g199,g202)
    c: InternalAlignment(g200,g202)
    c: InternalAlignment(g201,g202)
    c: InternalAlignment(g203,g202)
    c: InternalAlignment(g204,g202)
    c: Block(g202)
    c: Block(g196)
    c: Coincident(g205,g202)
    c: Coincident(g205,g37)
    c: Coincident(g206,g37)
    c: Coincident(g206,g196)
    c: Coincident(g207,g196)
    c: Coincident(g207,g202)
    c: Vertical(g207)
    c: Weight(g208) = 1
    c: Equal(g208,g209)
    c: Equal(g208,g210)
    c: InternalAlignment(g208,g211)
    c: InternalAlignment(g209,g211)
    c: InternalAlignment(g210,g211)
    c: InternalAlignment(g212,g211)
    c: InternalAlignment(g213,g211)
    c: Weight(g214) = 1
    c: Equal(g214,g215)
    c: Equal(g214,g216)
    c: InternalAlignment(g214,g217)
    c: InternalAlignment(g215,g217)
    c: InternalAlignment(g216,g217)
    c: InternalAlignment(g218,g217)
    c: InternalAlignment(g219,g217)
    c: Block(g217)
    c: Block(g211)
    c: Coincident(g220,g211)
    c: Coincident(g220,g43)
    c: Coincident(g221,g43)
    c: Coincident(g221,g217)
    c: Coincident(g222,g217)
    c: Coincident(g222,g211)
    c: Vertical(g222)
    c: Horizontal(g223)
    c: Block(g223)
    c: Vertical(g224)
    c: Block(g224)
    c: Block(g225)
    c: Weight(g226) = 1
    c: Equal(g226,g227)
    c: Equal(g226,g228)
    c: InternalAlignment(g226,g229)
    c: InternalAlignment(g227,g229)
    c: InternalAlignment(g228,g229)
    c: InternalAlignment(g230,g229)
    c: InternalAlignment(g231,g229)
    c: Weight(g232) = 1
    c: Equal(g232,g233)
    c: Equal(g232,g234)
    c: InternalAlignment(g232,g235)
    c: InternalAlignment(g233,g235)
    c: InternalAlignment(g234,g235)
    c: InternalAlignment(g236,g235)
    c: InternalAlignment(g237,g235)
    c: Weight(g238) = 1
    c: Equal(g238,g239)
    c: Equal(g238,g240)
    c: InternalAlignment(g238,g241)
    c: InternalAlignment(g239,g241)
    c: InternalAlignment(g240,g241)
    c: InternalAlignment(g242,g241)
    c: InternalAlignment(g243,g241)
    c: Weight(g244) = 1
    c: Equal(g244,g245)
    c: Equal(g244,g246)
    c: InternalAlignment(g244,g247)
    c: InternalAlignment(g245,g247)
    c: InternalAlignment(g246,g247)
    c: InternalAlignment(g248,g247)
    c: InternalAlignment(g249,g247)
    c: Block(g229)
    c: Block(g235)
    c: Block(g241)
    c: Block(g247)
    c: Coincident(g250,g235)
    c: Coincident(g250,g229)
    c: Horizontal(g250)
    c: Block(g192)
    c: Weight(g251) = 1
    c: Equal(g251,g252)
    c: Equal(g251,g253)
    c: InternalAlignment(g251,g254)
    c: InternalAlignment(g252,g254)
    c: InternalAlignment(g253,g254)
    c: InternalAlignment(g255,g254)
    c: InternalAlignment(g256,g254)
    c: Weight(g257) = 1
    c: Equal(g257,g258)
    c: Equal(g257,g259)
    c: InternalAlignment(g257,g260)
    c: InternalAlignment(g258,g260)
    c: InternalAlignment(g259,g260)
    c: InternalAlignment(g261,g260)
    c: InternalAlignment(g262,g260)
    c: Block(g254)
    c: Block(g260)
    c: Coincident(g263,g254)
    c: Coincident(g263,g260)
    c: Weight(g264) = 1
    c: Equal(g264,g265)
    c: Equal(g264,g266)
    c: InternalAlignment(g264,g267)
    c: InternalAlignment(g265,g267)
    c: InternalAlignment(g266,g267)
    c: InternalAlignment(g268,g267)
    c: InternalAlignment(g269,g267)
    c: Weight(g270) = 1
    c: Equal(g270,g271)
    c: Equal(g270,g272)
    c: InternalAlignment(g270,g273)
    c: InternalAlignment(g271,g273)
    c: InternalAlignment(g272,g273)
    c: InternalAlignment(g274,g273)
    c: InternalAlignment(g275,g273)
    c: Weight(g276) = 1
    c: Equal(g276,g277)
    c: Equal(g276,g278)
    c: InternalAlignment(g276,g279)
    c: InternalAlignment(g277,g279)
    c: InternalAlignment(g278,g279)
    c: InternalAlignment(g280,g279)
    c: InternalAlignment(g281,g279)
    c: Block(g279)
    c: Block(g273)
    c: Block(g267)
    c: Coincident(g282,g273)
    c: Coincident(g282,g267)
    c: Coincident(g283,g267)
    c: Coincident(g283,g279)
    c: Vertical(g283)
    c: Coincident(g284,g279)
    c: Coincident(g284,g273)
    c: Horizontal(g284)
    c: Weight(g285) = 1
    c: Equal(g285,g286)
    c: InternalAlignment(g285,g287)
    c: InternalAlignment(g286,g287)
    c: InternalAlignment(g288,g287)
    c: InternalAlignment(g289,g287)
    c: Weight(g290) = 1
    c: InternalAlignment(g291,g293)
    c: InternalAlignment(g292,g293)
    c: InternalAlignment(g294,g293)
    c: InternalAlignment(g295,g293)
    c: Weight(g296) = 1
    c: Equal(g296,g297)
    c: Equal(g296,g298)
    c: InternalAlignment(g296,g299)
    c: InternalAlignment(g297,g299)
    c: InternalAlignment(g298,g299)
    c: InternalAlignment(g300,g299)
    c: InternalAlignment(g301,g299)
    c: Equal(g302,g303)
    c: Equal(g302,g304)
    c: InternalAlignment(g302,g305)
    c: InternalAlignment(g303,g305)
    c: InternalAlignment(g304,g305)
    c: InternalAlignment(g306,g305)
    c: InternalAlignment(g307,g305)
    c: Block(g293)
    c: Block(g299)
    c: Block(g305)
    c: Block(g287)
    c: Coincident(g308,g287)
    c: Coincident(g308,g293)
    c: Horizontal(g308)
    c: Coincident(g309,g293)
    c: Coincident(g309,g299)
    c: Vertical(g309)
    c: Coincident(g310,g299)
    c: Coincident(g310,g305)
    c: Horizontal(g310)
    c: Coincident(g311,g305)
    c: Coincident(g311,g287)
    c: Weight(g312) = 1
    c: Equal(g312,g313)
    c: Equal(g312,g314)
    c: InternalAlignment(g312,g315)
    c: InternalAlignment(g313,g315)
    c: InternalAlignment(g314,g315)
    c: InternalAlignment(g316,g315)
    c: InternalAlignment(g317,g315)
    c: Weight(g318) = 1
    c: Equal(g318,g319)
    c: Equal(g318,g320)
    c: InternalAlignment(g318,g321)
    c: InternalAlignment(g319,g321)
    c: InternalAlignment(g320,g321)
    c: InternalAlignment(g322,g321)
    c: InternalAlignment(g323,g321)
    c: Weight(g324) = 1
    c: Equal(g324,g325)
    c: Equal(g324,g326)
    c: InternalAlignment(g324,g327)
    c: InternalAlignment(g325,g327)
    c: InternalAlignment(g326,g327)
    c: InternalAlignment(g328,g327)
    c: InternalAlignment(g329,g327)
    c: Block(g327)
    c: Block(g321)
    c: Block(g315)
    c: Coincident(g330,g327)
    c: Coincident(g330,g321)
    c: Horizontal(g330)
    c: Coincident(g331,g321)
    c: Coincident(g331,g315)
    c: Vertical(g331)
    c: Coincident(g332,g315)
    c: Coincident(g332,g327)
    c: InternalAlignment(g333,g334)
    c: InternalAlignment(g335,g334)
    c: InternalAlignment(g336,g334)
    c: Block(g334)
    c: Equal(g337,g338)
    c: Equal(g337,g339)
    c: InternalAlignment(g337,g340)
    c: InternalAlignment(g338,g340)
    c: InternalAlignment(g339,g340)
    c: InternalAlignment(g341,g340)
    c: InternalAlignment(g342,g340)
    c: Block(g340)
    c: Coincident(g343,g334)
    c: Horizontal(g343)
    c: Block(g343)
    c: Coincident(g344,g334)
    c: Coincident(g344,g260)
    c: Vertical(g344)
    c: Coincident(g345,g340)
    c: Coincident(g345,g254)
    c: Vertical(g345)
    c: Coincident(g347,g5)
    c: Coincident(g348,g5)
    c: Block(g346)
    c: Block(g5)
    c: Block(g348)
    c: Block(g347)
FEATURE [Sketcher::SketchObject] Sketch001
  FullyConstrained = true
  MapMode = 4
  Placement = pos=(0,0,0) rot=(0.57735,0.57735,0.57735;2.0944rad)
  Support = -> [Sketch]
  sketch-geometry (46):
    g0: BSplineCurve PolesCount=3 KnotsCount=2 Degree=2 IsPeriodic=0
    g1: ArcOfCircle CenterX=73.1223 CenterY=-32.291 CenterZ=0 NormalX=0 NormalY=0 NormalZ=1 AngleXU=0 Radius=13 StartAngle=5.92268 EndAngle=9.06428
    g2: ArcOfCircle CenterX=66.7816 CenterY=-49.1439 CenterZ=0 NormalX=0 NormalY=0 NormalZ=1 AngleXU=0 Radius=13 StartAngle=2.78068 EndAngle=5.92131
    g3: ArcOfCircle CenterX=55.9263 CenterY=-78.1807 CenterZ=0 NormalX=0 NormalY=0 NormalZ=1 AngleXU=0 Radius=13 StartAngle=5.92268 EndAngle=9.06428
    g4: ArcOfCircle CenterX=49.5884 CenterY=-95.0342 CenterZ=0 NormalX=0 NormalY=0 NormalZ=1 AngleXU=0 Radius=13 StartAngle=2.78068 EndAngle=5.92131
    g5: ArcOfCircle CenterX=38.7206 CenterY=-124.067 CenterZ=0 NormalX=0 NormalY=0 NormalZ=1 AngleXU=0 Radius=13 StartAngle=5.92268 EndAngle=9.06428
    g6: ArcOfCircle CenterX=32.3875 CenterY=-140.92 CenterZ=0 NormalX=0 NormalY=0 NormalZ=1 AngleXU=0 Radius=13 StartAngle=2.78068 EndAngle=5.92131
    g7: ArcOfCircle CenterX=21.4715 CenterY=-169.934 CenterZ=0 NormalX=0 NormalY=0 NormalZ=1 AngleXU=0 Radius=13 StartAngle=5.92268 EndAngle=9.06428
    g8: ArcOfCircle CenterX=15.1336 CenterY=-186.787 CenterZ=0 NormalX=0 NormalY=0 NormalZ=1 AngleXU=0 Radius=13 StartAngle=2.78068 EndAngle=5.92131
    g9-g12: Circle x4 (B-spline internal-alignment scaffolding for g13; pole/knot coordinates omitted)
    g13: BSplineCurve PolesCount=4 KnotsCount=2 Degree=3 IsPeriodic=0
    g14: GeomPoint X=28.8094 Y=-19.0875 Z=0
    g15: GeomPoint X=47.0443 Y=-50.4712 Z=0
    g16: Circle CenterX=53.5586 CenterY=-23.2695 CenterZ=0 NormalX=0 NormalY=0 NormalZ=1 AngleXU=0 Radius=3.24518
    g17: Circle CenterX=-195.441 CenterY=-127.082 CenterZ=0 NormalX=0 NormalY=0 NormalZ=1 AngleXU=0 Radius=1
    g18: Circle CenterX=-8.24091 CenterY=-197.481 CenterZ=0 NormalX=0 NormalY=0 NormalZ=1 AngleXU=0 Radius=1
    g19: Circle CenterX=12.8789 CenterY=-141.321 CenterZ=0 NormalX=0 NormalY=0 NormalZ=1 AngleXU=0 Radius=1
    g20: BSplineCurve PolesCount=3 KnotsCount=2 Degree=2 IsPeriodic=0
    g21: GeomPoint X=-195.441 Y=-127.082 Z=0
    g22: GeomPoint X=12.8789 Y=-141.321 Z=0
    g23: Circle CenterX=-12.8016 CenterY=-179.036 CenterZ=0 NormalX=0 NormalY=0 NormalZ=1 AngleXU=0 Radius=10.5072
    g24: Circle CenterX=0.933922 CenterY=-166.43 CenterZ=0 NormalX=0 NormalY=0 NormalZ=1 AngleXU=0 Radius=3.26661
    g25: Circle CenterX=-33.5518 CenterY=-176.44 CenterZ=0 NormalX=0 NormalY=0 NormalZ=1 AngleXU=0 Radius=5.64388
    g26: Circle CenterX=-47.2366 CenterY=-173.859 CenterZ=0 NormalX=0 NormalY=0 NormalZ=1 AngleXU=0 Radius=3.01653
    g27: Circle CenterX=-56.2595 CenterY=-171.456 CenterZ=0 NormalX=0 NormalY=0 NormalZ=1 AngleXU=0 Radius=2.12826
    g28: ArcOfCircle CenterX=51.2151 CenterY=-198.473 CenterZ=0 NormalX=0 NormalY=0 NormalZ=1 AngleXU=0 Radius=20 StartAngle=2.78189 EndAngle=4.35269
    g29: LineSegment StartX=32.4951 StartY=-191.433 StartZ=0 EndX=94.6578 EndY=-26.1352 EndZ=0
    g30: LineSegment StartX=43.1192 StartY=-220.001 StartZ=0 EndX=-196.497 EndY=-129.89 EndZ=0
    g31: LineSegment StartX=43.1192 StartY=-220.001 StartZ=0 EndX=44.1752 EndY=-217.193 EndZ=0
    g32: LineSegment StartX=117.223 StartY=-19.0875 StartZ=0 EndX=117.223 EndY=-16.0875 EndZ=0
    g33: LineSegment StartX=117.223 StartY=-16.0875 StartZ=0 EndX=17.2232 EndY=-16.0875 EndZ=0
    g34: LineSegment StartX=17.2232 StartY=-16.0875 StartZ=0 EndX=17.2232 EndY=-19.0875 EndZ=0
    g35: LineSegment StartX=28.8094 StartY=-19.0875 StartZ=0 EndX=17.2232 EndY=-19.0875 EndZ=0
    g36: LineSegment StartX=47.0443 StartY=-50.4712 StartZ=0 EndX=12.8789 EndY=-141.321 EndZ=0
    g37: LineSegment StartX=-195.441 StartY=-127.082 StartZ=0 EndX=-196.497 EndY=-129.89 EndZ=0
    g38: LineSegment StartX=85.2866 StartY=-36.8766 StartZ=0 EndX=78.9396 EndY=-53.7463 EndZ=0
    g39: LineSegment StartX=60.9579 StartY=-27.7053 StartZ=0 EndX=54.6191 EndY=-44.5532 EndZ=0
    g40: LineSegment StartX=68.0907 StartY=-82.7664 StartZ=0 EndX=61.7465 EndY=-99.6365 EndZ=0
    g41: LineSegment StartX=43.7619 StartY=-73.595 StartZ=0 EndX=37.426 EndY=-90.4435 EndZ=0
    g42: LineSegment StartX=50.885 StartY=-128.652 StartZ=0 EndX=44.5456 EndY=-145.522 EndZ=0
    g43: LineSegment StartX=26.5562 StartY=-119.481 StartZ=0 EndX=20.2251 EndY=-136.329 EndZ=0
    g44: LineSegment StartX=9.3071 StartY=-165.349 StartZ=0 EndX=2.97115 EndY=-182.197 EndZ=0
    g45: LineSegment StartX=33.6358 StartY=-174.52 StartZ=0 EndX=27.2917 EndY=-191.39 EndZ=0
  constraints (71):
    c: Block(g0)
    c: Block(g1)
    c: Block(g2)
    c: Block(g4)
    c: Block(g3)
    c: Block(g6)
    c: Block(g5)
    c: Block(g8)
    c: Block(g7)
    c: Weight(g9) = 1
    c: Equal(g9,g10)
    c: Equal(g9,g11)
    c: Equal(g9,g12)
    c: InternalAlignment(g9-g12 -> g13) x4
    c: InternalAlignment(g14,g13)
    c: InternalAlignment(g15,g13)
    c: Block(g16)
    c: Weight(g17) = 1
    c: Equal(g17,g18)
    c: Equal(g17,g19)
    c: InternalAlignment(g17,g20)
    c: InternalAlignment(g18,g20)
    c: InternalAlignment(g19,g20)
    c: InternalAlignment(g21,g20)
    c: InternalAlignment(g22,g20)
    c: Block(g20)
    c: Block(g23)
    c: Block(g24)
    c: Block(g25)
    c: Block(g26)
    c: Block(g27)
    c: Block(g28)
    c: Coincident(g29,g28)
    c: Coincident(g29,g0)
    c: Block(g13)
    c: Coincident(g31,g30)
    c: Coincident(g31,g28)
    c: Block(g31)
    c: Coincident(g32,g0)
    c: Vertical(g32)
    c: Coincident(g33,g32)
    c: Horizontal(g33)
    c: Coincident(g34,g33)
    c: Vertical(g34)
    c: Block(g33)
    c: Coincident(g35,g13)
    c: Coincident(g35,g34)
    c: Horizontal(g35)
    c: Coincident(g36,g13)
    c: Coincident(g36,g20)
    c: Coincident(g37,g20)
    c: Coincident(g37,g30)
    c: Block(g30)
    c: Coincident(g38,g1)
    c: Coincident(g38,g2)
    c: Coincident(g39,g1)
    c: Coincident(g39,g2)
    c: Coincident(g40,g3)
    c: Coincident(g40,g4)
    c: Coincident(g41,g3)
    c: Coincident(g41,g4)
    c: Coincident(g42,g5)
    c: Coincident(g42,g6)
    c: Coincident(g43,g5)
    c: Coincident(g43,g6)
    c: Coincident(g44,g7)
    c: Coincident(g44,g8)
    c: Coincident(g45,g7)
    c: Coincident(g45,g8)
    c: Distance(g30) = 256
    c: Distance(g33) = 100
FEATURE [Part::Extrusion] Extrude002
  Base = -> Sketch001
  Dir = (1,0,0)
  DirMode = 2
  FaceMakerClass = Part::FaceMakerBullseye
  LengthFwd = 8
  LengthRev = 0
  Solid = true
  Symmetric = false
FEATURE [Sketcher::SketchObject] Sketch002
  FullyConstrained = true
  sketch-geometry (20):
    g0: LineSegment StartX=-2.77179 StartY=-200.304 StartZ=0 EndX=5.22821 EndY=-200.304 EndZ=0
    g1: LineSegment StartX=5.22821 StartY=-200.304 StartZ=0 EndX=5.22821 EndY=-197.304 EndZ=0
    g2: LineSegment StartX=-2.77179 StartY=-200.304 StartZ=0 EndX=-2.77179 EndY=-197.304 EndZ=0
    g3: LineSegment StartX=5.22821 StartY=-197.304 StartZ=0 EndX=8.22821 EndY=-197.304 EndZ=0
    g4: LineSegment StartX=-2.77179 StartY=-197.304 StartZ=0 EndX=-5.77179 EndY=-197.304 EndZ=0
    g5: LineSegment StartX=19.2282 StartY=-203.304 StartZ=0 EndX=19.2282 EndY=-206.304 EndZ=0
    g6: LineSegment StartX=-16.7718 StartY=-203.304 StartZ=0 EndX=-16.7718 EndY=-206.304 EndZ=0
    g7: LineSegment StartX=-16.7718 StartY=-206.304 StartZ=0 EndX=19.2282 EndY=-206.304 EndZ=0
    g8: Circle CenterX=-16.7718 CenterY=-203.304 CenterZ=0 NormalX=0 NormalY=0 NormalZ=1 AngleXU=0 Radius=1
    g9: Circle CenterX=-5.77179 CenterY=-203.304 CenterZ=0 NormalX=0 NormalY=0 NormalZ=1 AngleXU=0 Radius=1
    g10: Circle CenterX=-5.77179 CenterY=-197.304 CenterZ=0 NormalX=0 NormalY=0 NormalZ=1 AngleXU=0 Radius=1
    g11: BSplineCurve PolesCount=3 KnotsCount=2 Degree=2 IsPeriodic=0
    g12: GeomPoint X=-16.7718 Y=-203.304 Z=0
    g13: GeomPoint X=-5.77179 Y=-197.304 Z=0
    g14: Circle CenterX=19.2282 CenterY=-203.304 CenterZ=0 NormalX=0 NormalY=0 NormalZ=1 AngleXU=0 Radius=1
    g15: Circle CenterX=8.22821 CenterY=-203.304 CenterZ=0 NormalX=0 NormalY=0 NormalZ=1 AngleXU=0 Radius=1
    g16: Circle CenterX=8.22821 CenterY=-197.304 CenterZ=0 NormalX=0 NormalY=0 NormalZ=1 AngleXU=0 Radius=1
    g17: BSplineCurve PolesCount=3 KnotsCount=2 Degree=2 IsPeriodic=0
    g18: GeomPoint X=19.2282 Y=-203.304 Z=0
    g19: GeomPoint X=8.22821 Y=-197.304 Z=0
  constraints (41):
    c: Horizontal(g0)
    c: Distance(g0) = 8
    c: Coincident(g1,g0)
    c: Vertical(g1)
    c: Distance(g1) = 3
    c: Coincident(g2,g0)
    c: Vertical(g2)
    c: Distance(g2) = 3
    c: Coincident(g3,g1)
    c: Horizontal(g3)
    c: Distance(g3) = 3
    c: Coincident(g4,g2)
    c: Horizontal(g4)
    c: Distance(g4) = 3
    c: Vertical(g5)
    c: Vertical(g6)
    c: Coincident(g7,g6)
    c: Coincident(g7,g5)
    c: Weight(g8) = 1
    c: Equal(g8,g9)
    c: Equal(g8,g10)
    c: Coincident(g11,g4)
    c: InternalAlignment(g8,g11)
    c: InternalAlignment(g9,g11)
    c: InternalAlignment(g10,g11)
    c: InternalAlignment(g12,g11)
    c: InternalAlignment(g13,g11)
    c: Coincident(g17,g5)
    c: Weight(g14) = 1
    c: Equal(g14,g15)
    c: Equal(g14,g16)
    c: Coincident(g17,g3)
    c: InternalAlignment(g14,g17)
    c: InternalAlignment(g15,g17)
    c: InternalAlignment(g16,g17)
    c: InternalAlignment(g18,g17)
    c: InternalAlignment(g19,g17)
    c: Block(g7)
    c: Block(g17)
    c: Block(g11)
    c: Block(g6)
FEATURE [Part::Extrusion] Extrude003
  Base = -> Sketch002
  Dir = (0,0,1)
  DirMode = 2
  FaceMakerClass = Part::FaceMakerBullseye
  LengthFwd = 260
  LengthRev = 0
  Solid = true
  Symmetric = false
FEATURE [Part::Extrusion] Extrude
  Base = -> Sketch
  Dir = (0,0,1)
  DirMode = 2
  FaceMakerClass = Part::FaceMakerBullseye
  LengthFwd = 14
  LengthRev = 0
  Solid = true
  Symmetric = false
